FCSTD DOCUMENT  (FreeCAD 1.0R39109 (Git))
Label: top_acylic
License: All rights reserved
LicenseURL: https://en.wikipedia.org/wiki/All_rights_reserved
objects: Sketcher::SketchObject×1, PartDesign::Body×1
note: 3 computed .brp shape members not serialized (recipe doc carries the construction recipe); baked Part::Feature solids carry a one-line shape summary decoded from their .brp

FEATURE [Sketcher::SketchObject] Sketch
  ArcFitTolerance = 1e-06
  AttachmentSupport = -> [XY_Plane]
  FullyConstrained = true
  MakeInternals = false
  MapMode = 5
  sketch-geometry (67):
    g0: LineSegment [constr] StartX=45 StartY=0 StartZ=0 EndX=255 EndY=0 EndZ=0
    g1: LineSegment [constr] StartX=300 StartY=22 StartZ=0 EndX=300 EndY=316 EndZ=0
    g2: LineSegment [constr] StartX=255 StartY=338 StartZ=0 EndX=45 EndY=338 EndZ=0
    g3: LineSegment [constr] StartX=0 StartY=316 StartZ=0 EndX=0 EndY=22 EndZ=0
    g4: Circle CenterX=150 CenterY=169 CenterZ=0 NormalX=0 NormalY=0 NormalZ=1 AngleXU=0 Radius=57.5
    g5: LineSegment [constr] StartX=300 StartY=22 StartZ=0 EndX=255 EndY=22 EndZ=0
    g6: LineSegment [constr] StartX=255 StartY=22 StartZ=0 EndX=255 EndY=0 EndZ=0
    g7: LineSegment [constr] StartX=255 StartY=338 StartZ=0 EndX=255 EndY=316 EndZ=0
    g8: LineSegment [constr] StartX=255 StartY=316 StartZ=0 EndX=300 EndY=316 EndZ=0
    g9: LineSegment [constr] StartX=45 StartY=338 StartZ=0 EndX=45 EndY=316 EndZ=0
    g10: LineSegment [constr] StartX=45 StartY=316 StartZ=0 EndX=0 EndY=316 EndZ=0
    g11: LineSegment [constr] StartX=0 StartY=22 StartZ=0 EndX=45 EndY=22 EndZ=0
    g12: LineSegment [constr] StartX=45 StartY=22 StartZ=0 EndX=45 EndY=0 EndZ=0
    g13: LineSegment [constr] StartX=10 StartY=22 StartZ=0 EndX=10 EndY=316 EndZ=0
    g14: Circle [constr] CenterX=10 CenterY=257.2 CenterZ=0 NormalX=0 NormalY=0 NormalZ=1 AngleXU=0 Radius=2.5
    g15: Circle [constr] CenterX=10 CenterY=169 CenterZ=0 NormalX=0 NormalY=0 NormalZ=1 AngleXU=0 Radius=2.5
    g16: Circle [constr] CenterX=10 CenterY=80.8 CenterZ=0 NormalX=0 NormalY=0 NormalZ=1 AngleXU=0 Radius=2.5
    g17: Circle [constr] CenterX=87 CenterY=10 CenterZ=0 NormalX=0 NormalY=0 NormalZ=1 AngleXU=0 Radius=2.5
    g18: Circle [constr] CenterX=213 CenterY=10 CenterZ=0 NormalX=0 NormalY=0 NormalZ=1 AngleXU=0 Radius=2.5
    g19: LineSegment [constr] StartX=255 StartY=328 StartZ=0 EndX=45 EndY=328 EndZ=0
    g20: LineSegment [constr] StartX=290 StartY=22 StartZ=0 EndX=290 EndY=316 EndZ=0
    g21: LineSegment [constr] StartX=255 StartY=10 StartZ=0 EndX=45 EndY=10 EndZ=0
    g22: Circle [constr] CenterX=290 CenterY=80.8 CenterZ=0 NormalX=0 NormalY=0 NormalZ=1 AngleXU=0 Radius=2.5
    g23: Circle [constr] CenterX=290 CenterY=169 CenterZ=0 NormalX=0 NormalY=0 NormalZ=1 AngleXU=0 Radius=2.5
    g24: Circle [constr] CenterX=290 CenterY=257.2 CenterZ=0 NormalX=0 NormalY=0 NormalZ=1 AngleXU=0 Radius=2.5
    g25: Circle [constr] CenterX=213 CenterY=328 CenterZ=0 NormalX=0 NormalY=0 NormalZ=1 AngleXU=0 Radius=2.5
    g26: Circle [constr] CenterX=87 CenterY=328 CenterZ=0 NormalX=0 NormalY=0 NormalZ=1 AngleXU=0 Radius=2.5
    g27: LineSegment StartX=40 StartY=279 StartZ=0 EndX=40 EndY=59 EndZ=0
    g28: LineSegment StartX=40 StartY=59 StartZ=0 EndX=260 EndY=59 EndZ=0
    g29: LineSegment StartX=260 StartY=59 StartZ=0 EndX=260 EndY=279 EndZ=0
    g30: LineSegment StartX=260 StartY=279 StartZ=0 EndX=40 EndY=279 EndZ=0
    g31: LineSegment [constr] StartX=60 StartY=259 StartZ=0 EndX=60 EndY=79 EndZ=0
    g32: LineSegment [constr] StartX=60 StartY=79 StartZ=0 EndX=240 EndY=79 EndZ=0
    g33: LineSegment [constr] StartX=240 StartY=79 StartZ=0 EndX=240 EndY=259 EndZ=0
    g34: LineSegment [constr] StartX=240 StartY=259 StartZ=0 EndX=60 EndY=259 EndZ=0
    g35: Circle CenterX=60 CenterY=79 CenterZ=0 NormalX=0 NormalY=0 NormalZ=1 AngleXU=0 Radius=2.5
    g36: Circle CenterX=60 CenterY=259 CenterZ=0 NormalX=0 NormalY=0 NormalZ=1 AngleXU=0 Radius=2.5
    g37: Circle CenterX=240 CenterY=259 CenterZ=0 NormalX=0 NormalY=0 NormalZ=1 AngleXU=0 Radius=2.5
    g38: Circle CenterX=240 CenterY=79 CenterZ=0 NormalX=0 NormalY=0 NormalZ=1 AngleXU=0 Radius=2.5
    g39: LineSegment [constr] StartX=63.75 StartY=255.25 StartZ=0 EndX=63.75 EndY=82.75 EndZ=0
    g40: LineSegment [constr] StartX=63.75 StartY=82.75 StartZ=0 EndX=236.25 EndY=82.75 EndZ=0
    g41: LineSegment [constr] StartX=236.25 StartY=82.75 StartZ=0 EndX=236.25 EndY=255.25 EndZ=0
    g42: LineSegment [constr] StartX=236.25 StartY=255.25 StartZ=0 EndX=63.75 EndY=255.25 EndZ=0
    g43: Circle CenterX=150 CenterY=82.75 CenterZ=0 NormalX=0 NormalY=0 NormalZ=1 AngleXU=0 Radius=2.75
    g44: Circle CenterX=236.25 CenterY=169 CenterZ=0 NormalX=0 NormalY=0 NormalZ=1 AngleXU=0 Radius=2.75
    g45: Circle CenterX=150 CenterY=255.25 CenterZ=0 NormalX=0 NormalY=0 NormalZ=1 AngleXU=0 Radius=2.75
    g46: Circle CenterX=63.75 CenterY=169 CenterZ=0 NormalX=0 NormalY=0 NormalZ=1 AngleXU=0 Radius=2.75
    g47: Circle [constr] CenterX=150 CenterY=169 CenterZ=0 NormalX=0 NormalY=0 NormalZ=1 AngleXU=0 Radius=81.25
    g48: Circle [constr] CenterX=220.5 CenterY=98.5 CenterZ=0 NormalX=0 NormalY=0 NormalZ=1 AngleXU=0 Radius=18.875
    g49: LineSegment [constr] StartX=220.5 StartY=98.5 StartZ=0 EndX=220.5 EndY=79 EndZ=0
    g50: LineSegment [constr] StartX=220.5 StartY=79 StartZ=0 EndX=240 EndY=79 EndZ=0
    g51: LineSegment [constr] StartX=240 StartY=79 StartZ=0 EndX=240 EndY=98.5 EndZ=0
    g52: LineSegment [constr] StartX=240 StartY=98.5 StartZ=0 EndX=220.5 EndY=98.5 EndZ=0
    g53: Circle CenterX=220.5 CenterY=98.5 CenterZ=0 NormalX=0 NormalY=0 NormalZ=1 AngleXU=0 Radius=4
    g54: Circle [constr] CenterX=220.5 CenterY=98.5 CenterZ=0 NormalX=0 NormalY=0 NormalZ=1 AngleXU=0 Radius=11
    g55: LineSegment [constr] StartX=255 StartY=0 StartZ=0 EndX=300 EndY=0 EndZ=0
    g56: LineSegment [constr] StartX=300 StartY=0 StartZ=0 EndX=300 EndY=22 EndZ=0
    g57: LineSegment [constr] StartX=255 StartY=338 StartZ=0 EndX=300 EndY=338 EndZ=0
    g58: LineSegment [constr] StartX=300 StartY=338 StartZ=0 EndX=300 EndY=316 EndZ=0
    g59: LineSegment [constr] StartX=0 StartY=316 StartZ=0 EndX=0 EndY=338 EndZ=0
    g60: LineSegment [constr] StartX=0 StartY=338 StartZ=0 EndX=45 EndY=338 EndZ=0
    g61: LineSegment [constr] StartX=0 StartY=0 StartZ=0 EndX=45 EndY=0 EndZ=0
    g62: LineSegment [constr] StartX=0 StartY=0 StartZ=0 EndX=0 EndY=22 EndZ=0
    g63: LineSegment [constr] StartX=0 StartY=22 StartZ=0 EndX=0 EndY=0 EndZ=0
    g64: LineSegment [constr] StartX=0 StartY=0 StartZ=0 EndX=45 EndY=0 EndZ=0
    g65: LineSegment [constr] StartX=300 StartY=0 StartZ=0 EndX=300 EndY=22 EndZ=0
    g66: LineSegment [constr] StartX=300 StartY=0 StartZ=0 EndX=300 EndY=22 EndZ=0
  constraints (185):
    c: Horizontal(g0)
    c: Horizontal(g2)
    c: Vertical(g1)
    c: Vertical(g3)
    c: Diameter(g4) = 115
    c: DistanceY(g-1,g4) = 169
    c: DistanceX(g-1,g4) = 150
    c: Horizontal(g5)
    c: Coincident(g5,g6)
    c: Vertical(g6)
    c: Vertical(g7)
    c: Coincident(g7,g8)
    c: Horizontal(g8)
    c: Vertical(g9)
    c: Coincident(g9,g10)
    c: Horizontal(g10)
    c: Horizontal(g11)
    c: Coincident(g11,g12)
    c: Vertical(g12)
    c: Horizontal(g11,g5)
    c: Horizontal(g7,g9)
    c: Vertical(g11,g9)
    c: Vertical(g5,g7)
    c: Coincident(g0,g12)
    c: Coincident(g3,g11)
    c: Coincident(g0,g6)
    c: Coincident(g1,g5)
    c: Coincident(g1,g8)
    c: Coincident(g2,g7)
    c: Coincident(g2,g9)
    c: Coincident(g3,g10)
    c: DistanceY(g-1,g2) = 338
    c: DistanceX(g-1,g1) = 300
    c: DistanceY(g6,g6) = 22
    c: Equal(g6,g7)
    c: DistanceX(g8,g8) = 45
    c: Equal(g8,g10)
    c: Horizontal(g0,g-1)
    c: Vertical(g3,g-1)
    c: PointOnObject(g13,g11)
    c: PointOnObject(g13,g10)
    c: Vertical(g13)
    c: DistanceX(g3,g13) = 10
    c: PointOnObject(g14,g13)
    c: Symmetric(g13,g13,g15)
    c: PointOnObject(g16,g13)
    c: Equal(g15,g14)
    c: Equal(g15,g16)
    c: Equal(g16,g17)
    c: Equal(g17,g18)
    c: Radius(g18) = 2.5
    c: Distance(g14,g13) = 58.8
    c: DistanceY(g13,g16) = 58.8
    c: PointOnObject(g19,g7)
    c: PointOnObject(g19,g9)
    c: Horizontal(g19)
    c: DistanceY(g19,g2) = 10
    c: PointOnObject(g20,g5)
    c: PointOnObject(g20,g8)
    c: Vertical(g20)
    c: DistanceX(g20,g1) = 10
    c: PointOnObject(g21,g6)
    c: PointOnObject(g21,g12)
    c: Horizontal(g21)
    c: DistanceY(g0,g21) = 10
    c: PointOnObject(g17,g21)
    c: PointOnObject(g18,g21)
    c: DistanceX(g18,g21) = 42
    c: DistanceX(g21,g17) = 42
    c: PointOnObject(g22,g20)
    c: PointOnObject(g23,g20)
    c: PointOnObject(g24,g20)
    c: PointOnObject(g25,g19)
    c: PointOnObject(g26,g19)
    c: Equal(g26,g25)
    c: Equal(g25,g24)
    c: Equal(g24,g23)
    c: Equal(g23,g22)
    c: Equal(g26,g14)
    c: Vertical(g26,g17)
    c: Vertical(g18,g25)
    c: Horizontal(g24,g14)
    c: Horizontal(g23,g15)
    c: Horizontal(g16,g22)
    c: Coincident(g27,g28)
    c: Coincident(g28,g29)
    c: Coincident(g29,g30)
    c: Coincident(g30,g27)
    c: Vertical(g27)
    c: Vertical(g29)
    c: Horizontal(g28)
    c: Horizontal(g30)
    c: Equal(g28,g29)
    c: DistanceX(g30,g30) = 220
    c: DistanceX(g27,g4) = 110
    c: DistanceY(g27,g4) = 110
    c: Coincident(g31,g32)
    c: Coincident(g32,g33)
    c: Coincident(g33,g34)
    c: Coincident(g34,g31)
    c: Vertical(g31)
    c: Vertical(g33)
    c: Horizontal(g32)
    c: Horizontal(g34)
    c: Equal(g33,g32)
    c: DistanceX(g32,g32) = 180
    c: DistanceX(g4,g32) = 90
    c: DistanceY(g31,g4) = 90
    c: Coincident(g35,g31)
    c: Coincident(g36,g31)
    c: Coincident(g37,g33)
    c: Coincident(g38,g32)
    c: Equal(g38,g37)
    c: Equal(g36,g37)
    c: Equal(g36,g35)
    c: Equal(g16,g35)
    c: Coincident(g39,g40)
    c: Coincident(g40,g41)
    c: Coincident(g41,g42)
    c: Coincident(g42,g39)
    c: Vertical(g39)
    c: Vertical(g41)
    c: Horizontal(g40)
    c: Horizontal(g42)
    c: DistanceX(g40,g40) = 172.5
    c: Equal(g40,g41)
    c: Symmetric(g40,g40,g43)
    c: Symmetric(g41,g41,g44)
    c: Symmetric(g42,g42,g45)
    c: Symmetric(g39,g39,g46)
    c: Equal(g46,g43)
    c: Equal(g43,g44)
    c: Equal(g44,g45)
    c: Diameter(g46) = 5.5
    c: DistanceY(g39,g4) = 86.25
    c: DistanceX(g4,g40) = 86.25
    c: Coincident(g47,g4)
    c: Diameter(g47) = 162.5
    c: Diameter(g48) = 37.75
    c: Coincident(g49,g50)
    c: Coincident(g50,g51)
    c: Coincident(g51,g52)
    c: Coincident(g52,g49)
    c: Vertical(g49)
    c: Vertical(g51)
    c: Horizontal(g50)
    c: Horizontal(g52)
    c: Coincident(g49,g48)
    c: Coincident(g50,g32)
    c: Equal(g52,g49)
    c: DistanceX(g52,g52) = 19.5
    c: Coincident(g53,g48)
    c: Diameter(g53) = 8
    c: Coincident(g54,g48)
    c: Diameter(g54) = 22
    c: Coincident(g55,g0)
    c: PointOnObject(g55,g-1)
    c: Coincident(g56,g55)
    c: Coincident(g56,g1)
    c: Vertical(g56)
    c: Coincident(g57,g2)
    c: Horizontal(g57)
    c: Coincident(g58,g57)
    c: Coincident(g58,g1)
    c: Vertical(g58)
    c: Coincident(g59,g3)
    c: PointOnObject(g59,g-2)
    c: Coincident(g60,g59)
    c: Coincident(g60,g2)
    c: Horizontal(g60)
    c: Coincident(g61,g-1)
    c: Coincident(g61,g0)
    c: Coincident(g62,g61)
    c: Coincident(g62,g3)
    c: PointOnObject(g63,g11)
    c: Vertical(g63)
    c: Coincident(g64,g63)
    c: PointOnObject(g64,g12)
    c: Horizontal(g64)
    c: Coincident(g63,g61)
    c: Coincident(g65,g55)
    c: Coincident(g65,g1)
    c: PointOnObject(g66,g55)
    c: Vertical(g66)
    c: Coincident(g66,g1)
FEATURE [PartDesign::Body] Body
  AllowCompound = false
  Group = -> [Sketch]
  Origin = -> Origin
